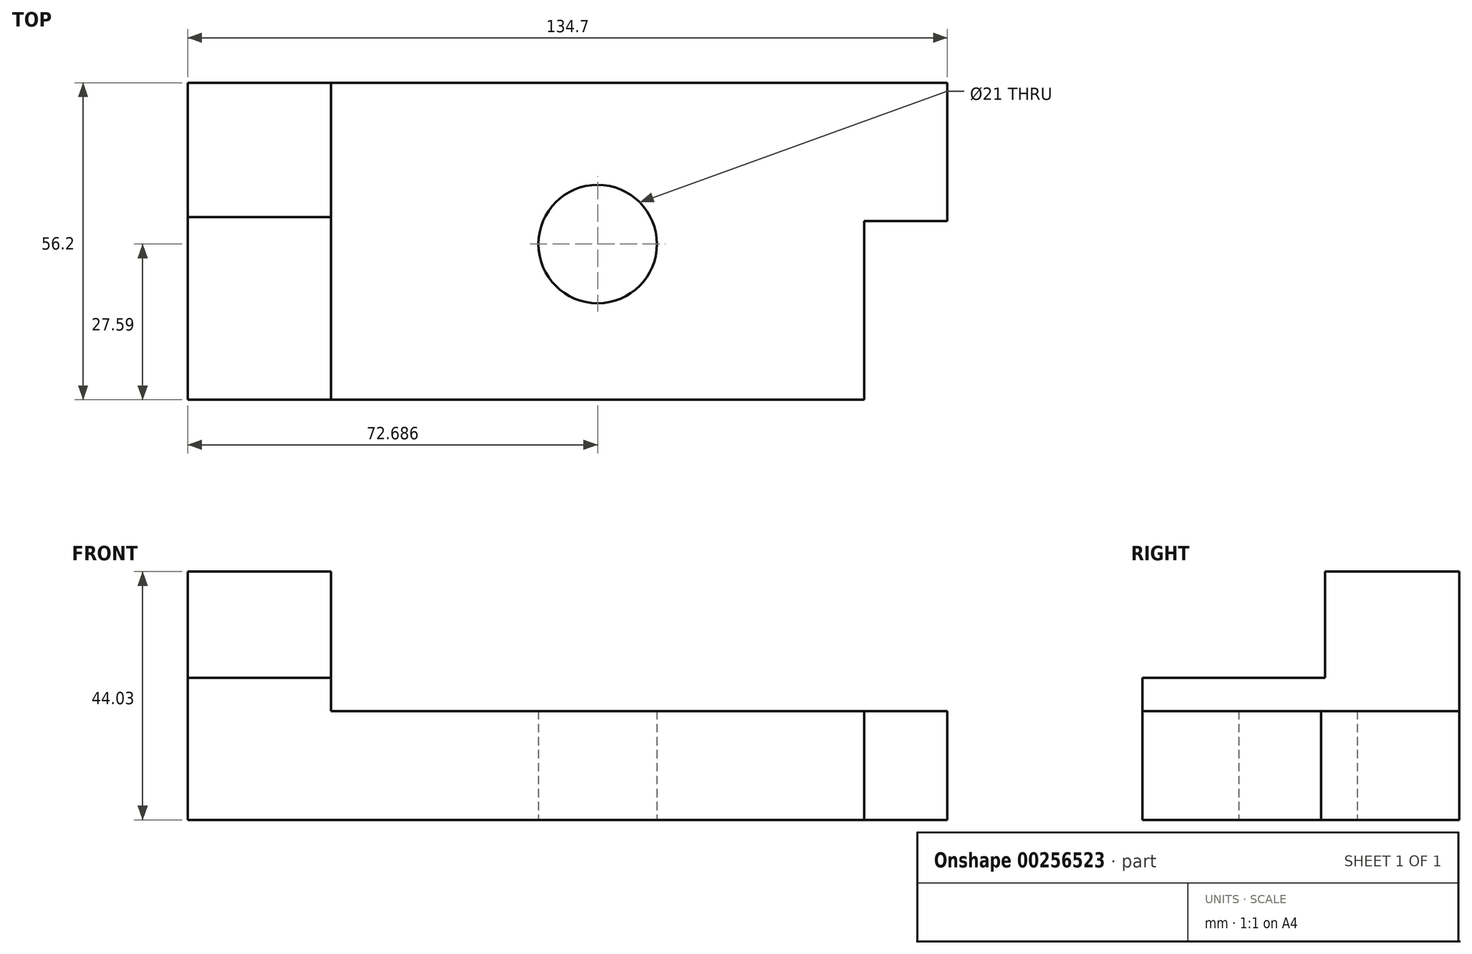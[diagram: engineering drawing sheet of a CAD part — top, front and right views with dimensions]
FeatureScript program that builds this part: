
annotation { "Feature Type Name" : "Feature", "Feature Type Description" : "" }
export const myFeature = defineFeature(function(context is Context, id is Id, definition is map)
    precondition{}
    {
        {
            var Q0;
            Q0=qCreatedBy(makeId("Top.planeOp"),FACE);
            var sketch = newSketch(context, id + "F0", { "sketchPlane" : qUnion([Q0])});
            skLineSegment(sketch, "E0.bottom", {"start": v(-34.95, 28.6) * mm, "end": v(59.62, 28.6) * mm});
            skLineSegment(sketch, "E0.top", {"start": v(-34.95, -27.59) * mm, "end": v(59.62, -27.59) * mm});
            skLineSegment(sketch, "E0.left", {"start": v(-34.95, 28.6) * mm, "end": v(-34.95, -27.59) * mm});
            skLineSegment(sketch, "E0.right", {"start": v(59.62, 28.6) * mm, "end": v(59.62, -27.59) * mm});
            skCircle(sketch, "E1", {"center": v(12.34, 0) * mm, "radius": 10.5 * mm});
            skPoint(sketch, "E1.centerSnap0", {"position": v(12.34, 28.6) * mm});
            skSolve(sketch);
        }
        {
            var Q0;
            Q0 = qSketchRegion(id + "F0", true);
            extrude(context, id + "F1", {"entities" : qUnion([Q0]), "depth" : 19.3 * mm});
        }
        {
            var Q0;
            Q0=makeQuery(id+"F1.opExtrude","SWEPT_FACE",FACE,{"disambiguationData":[OSD([sQuery(id+"F0.wireOp",EDGE,"E0.left")])]});
            var sketch = newSketch(context, id + "F2", { "sketchPlane" : qUnion([Q0])});
            skLineSegment(sketch, "E2.bottom", {"start": v(-28.6, 25.18) * mm, "end": v(27.59, 25.18) * mm});
            skLineSegment(sketch, "E2.top", {"start": v(-28.6, 0) * mm, "end": v(27.59, 0) * mm});
            skLineSegment(sketch, "E2.left", {"start": v(-28.6, 25.18) * mm, "end": v(-28.6, 0) * mm});
            skLineSegment(sketch, "E2.right", {"start": v(27.59, 25.18) * mm, "end": v(27.59, 0) * mm});
            skLineSegment(sketch, "E3.bottom", {"start": v(-28.6, 25.18) * mm, "end": v(-4.8, 25.18) * mm});
            skLineSegment(sketch, "E3.top", {"start": v(-28.6, 44.03) * mm, "end": v(-4.8, 44.03) * mm});
            skLineSegment(sketch, "E3.left", {"start": v(-28.6, 25.18) * mm, "end": v(-28.6, 44.03) * mm});
            skLineSegment(sketch, "E3.right", {"start": v(-4.8, 25.18) * mm, "end": v(-4.8, 44.03) * mm});
            skSolve(sketch);
        }
        {
            var Q0;
            Q0 = qSketchRegion(id + "F2", true);
            extrude(context, id + "F3", {"entities" : qUnion([Q0]), "operationType" : NewBodyOperationType.ADD, "depth" : 25.4 * mm});
        }
        {
            var Q0;
            Q0=makeQuery(id+"F1.opExtrude","SWEPT_FACE",FACE,{"disambiguationData":[OSD([sQuery(id+"F0.wireOp",EDGE,"E0.right")])]});
            var sketch = newSketch(context, id + "F4", { "sketchPlane" : qUnion([Q0])});
            skLineSegment(sketch, "E4.bottom", {"start": v(4.11, 19.3) * mm, "end": v(28.6, 19.3) * mm});
            skLineSegment(sketch, "E4.top", {"start": v(4.11, 0) * mm, "end": v(28.6, 0) * mm});
            skLineSegment(sketch, "E4.left", {"start": v(4.11, 19.3) * mm, "end": v(4.11, 0) * mm});
            skLineSegment(sketch, "E4.right", {"start": v(28.6, 19.3) * mm, "end": v(28.6, 0) * mm});
            skSolve(sketch);
        }
        {
            var Q0;
            Q0 = qSketchRegion(id + "F4", true);
            extrude(context, id + "F5", {"entities" : qUnion([Q0]), "operationType" : NewBodyOperationType.ADD, "depth" : 14.73 * mm});
        }
    });
